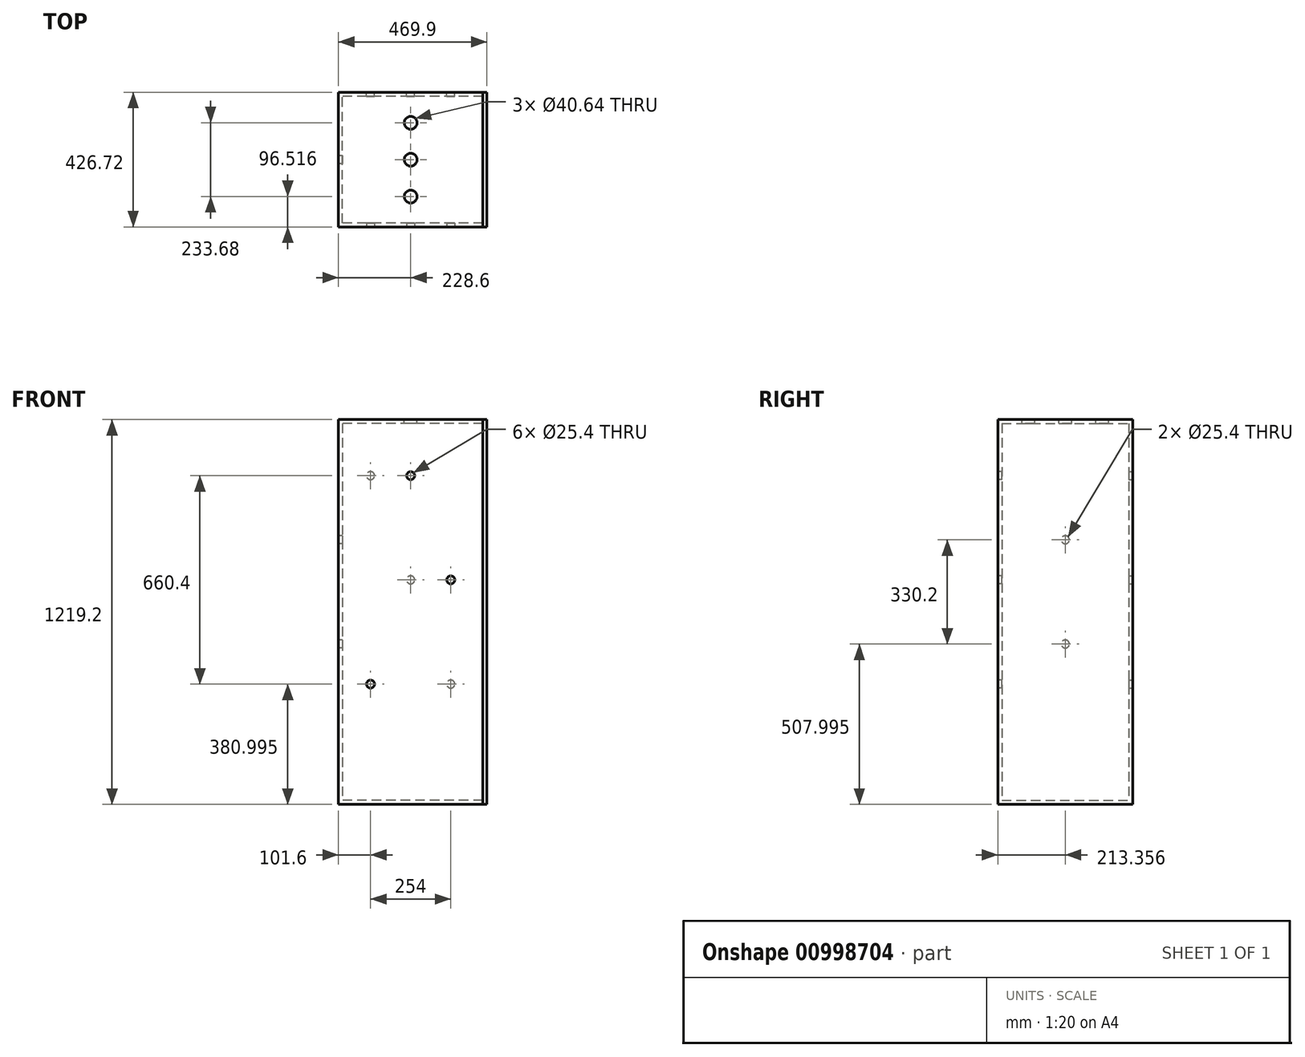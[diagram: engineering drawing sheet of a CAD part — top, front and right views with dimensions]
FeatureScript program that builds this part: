
annotation { "Feature Type Name" : "Feature", "Feature Type Description" : "" }
export const myFeature = defineFeature(function(context is Context, id is Id, definition is map)
    precondition{}
    {
        {
            var Q0;
            Q0=qCreatedBy(makeId("Right.planeOp"),FACE);
            var sketch = newSketch(context, id + "F0", { "sketchPlane" : qUnion([Q0])});
            skLineSegment(sketch, "E0.bottom", {"start": v(-375.54, 610.15) * mm, "end": v(51.18, 610.15) * mm});
            skLineSegment(sketch, "E0.top", {"start": v(-375.54, -609.05) * mm, "end": v(51.18, -609.05) * mm});
            skLineSegment(sketch, "E0.left", {"start": v(-375.54, 610.15) * mm, "end": v(-375.54, -609.05) * mm});
            skLineSegment(sketch, "E0.right", {"start": v(51.18, 610.15) * mm, "end": v(51.18, -609.05) * mm});
            skSolve(sketch);
        }
        {
            var Q0;
            Q0 = qSketchRegion(id + "F0", true);
            extrude(context, id + "F1", {"entities" : qUnion([Q0]), "depth" : 457.2 * mm, "offsetDistance" : 25.4 * mm});
        }
        {
            var Q0;
            Q0=makeQuery(id+"F1.opExtrude","CAP_FACE",FACE,{"disambiguationData":[OSD([sQuery(id+"F0.wireOp",EDGE,"E0.bottom"),sQuery(id+"F0.wireOp",EDGE,"E0.top"),sQuery(id+"F0.wireOp",EDGE,"E0.left"),sQuery(id+"F0.wireOp",EDGE,"E0.right")])],"isStart":false});
            shell(context, id + "F2", {"entities" : qUnion([Q0]), "thickness" : 12.7 * mm});
        }
        {
            var Q0;
            Q0=makeQuery(id+"F1.opExtrude","SWEPT_FACE",FACE,{"disambiguationData":[OSD([sQuery(id+"F0.wireOp",EDGE,"E0.bottom")])]});
            var sketch = newSketch(context, id + "F3", { "sketchPlane" : qUnion([Q0])});
            skLineSegment(sketch, "E1", {"start": v(228.6, 51.18) * mm, "end": v(228.6, -375.54) * mm, "construction": true});
            skLineSegment(sketch, "E2", {"start": v(228.6, -375.54) * mm, "end": v(228.6, -279.02) * mm, "construction": true});
            skCircle(sketch, "E3", {"center": v(228.6, -279.02) * mm, "radius": 20.32 * mm});
            skLineSegment(sketch, "E4", {"start": v(0, -162.18) * mm, "end": v(457.2, -162.18) * mm, "construction": true});
            skCircle(sketch, "E5.MirrorC", {"center": v(228.6, -45.34) * mm, "radius": 20.32 * mm});
            skCircle(sketch, "E6", {"center": v(228.6, -162.18) * mm, "radius": 20.32 * mm});
            skSolve(sketch);
        }
        {
            var Q0;
            Q0=sQuery(id+"F3.wireOp",VERTEX,"E6.center");
            var Q1;
            Q1=makeQuery(id+"F1.opExtrude","SWEPT_BODY",BODY,{"disambiguationData":[OSD([sQuery(id+"F0.wireOp",EDGE,"E0.bottom"),sQuery(id+"F0.wireOp",EDGE,"E0.top"),sQuery(id+"F0.wireOp",EDGE,"E0.left"),sQuery(id+"F0.wireOp",EDGE,"E0.right")])]});
            hole(context, id + "F4", {"style" : HoleStyle.SIMPLE, "endStyle" : HoleEndStyle.BLIND, "holeDiameter" : 40.64 * mm, "majorDiameter" : 6.35 * mm, "holeDepth" : 12.7 * mm, "isTappedThrough" : true, "tappedDepth" : 12.7 * mm, "tapClearance" : 3, "locations" : qUnion([Q0]), "scope" : qUnion([Q1])});
        }
        {
            var Q0;
            Q0=sQuery(id+"F3.wireOp",VERTEX,"E5.MirrorC.center");
            var Q1;
            Q1=makeQuery(id+"F1.opExtrude","SWEPT_BODY",BODY,{"disambiguationData":[OSD([sQuery(id+"F0.wireOp",EDGE,"E0.bottom"),sQuery(id+"F0.wireOp",EDGE,"E0.top"),sQuery(id+"F0.wireOp",EDGE,"E0.left"),sQuery(id+"F0.wireOp",EDGE,"E0.right")])]});
            hole(context, id + "F5", {"style" : HoleStyle.SIMPLE, "endStyle" : HoleEndStyle.BLIND, "holeDiameter" : 40.64 * mm, "majorDiameter" : 6.35 * mm, "holeDepth" : 12.7 * mm, "isTappedThrough" : true, "tappedDepth" : 12.7 * mm, "tapClearance" : 3, "locations" : qUnion([Q0]), "scope" : qUnion([Q1])});
        }
        {
            var Q0;
            Q0=sQuery(id+"F3.wireOp",VERTEX,"E2.end");
            var Q1;
            Q1=makeQuery(id+"F1.opExtrude","SWEPT_BODY",BODY,{"disambiguationData":[OSD([sQuery(id+"F0.wireOp",EDGE,"E0.bottom"),sQuery(id+"F0.wireOp",EDGE,"E0.top"),sQuery(id+"F0.wireOp",EDGE,"E0.left"),sQuery(id+"F0.wireOp",EDGE,"E0.right")])]});
            hole(context, id + "F6", {"style" : HoleStyle.SIMPLE, "endStyle" : HoleEndStyle.BLIND, "holeDiameter" : 40.64 * mm, "majorDiameter" : 6.35 * mm, "holeDepth" : 12.7 * mm, "isTappedThrough" : true, "tappedDepth" : 12.7 * mm, "tapClearance" : 3, "locations" : qUnion([Q0]), "scope" : qUnion([Q1])});
        }
        {
            var Q0;
            Q0=makeQuery(id+"F1.opExtrude","CAP_FACE",FACE,{"disambiguationData":[OSD([sQuery(id+"F0.wireOp",EDGE,"E0.bottom"),sQuery(id+"F0.wireOp",EDGE,"E0.top"),sQuery(id+"F0.wireOp",EDGE,"E0.left"),sQuery(id+"F0.wireOp",EDGE,"E0.right")])],"isStart":false});
            var sketch = newSketch(context, id + "F7", { "sketchPlane" : qUnion([Q0])});
            skLineSegment(sketch, "E7.bottom", {"start": v(-375.54, 610.15) * mm, "end": v(51.18, 610.15) * mm});
            skLineSegment(sketch, "E7.top", {"start": v(-375.54, -609.05) * mm, "end": v(51.18, -609.05) * mm});
            skLineSegment(sketch, "E7.left", {"start": v(-375.54, 610.15) * mm, "end": v(-375.54, -609.05) * mm});
            skLineSegment(sketch, "E7.right", {"start": v(51.18, 610.15) * mm, "end": v(51.18, -609.05) * mm});
            skSolve(sketch);
        }
        {
            var Q0;
            Q0 = qSketchRegion(id + "F7", true);
            extrude(context, id + "F8", {"entities" : qUnion([Q0]), "depth" : 12.7 * mm, "offsetDistance" : 25.4 * mm});
        }
        {
            var Q0;
            Q0=makeQuery(id+"F1.opExtrude","SWEPT_FACE",FACE,{"disambiguationData":[OSD([sQuery(id+"F0.wireOp",EDGE,"E0.left")])]});
            var sketch = newSketch(context, id + "F9", { "sketchPlane" : qUnion([Q0])});
            skLineSegment(sketch, "E8", {"start": v(0, 610.15) * mm, "end": v(101.6, 610.15) * mm, "construction": true});
            skLineSegment(sketch, "E9", {"start": v(101.6, 610.15) * mm, "end": v(355.6, 610.15) * mm, "construction": true});
            skLineSegment(sketch, "E10", {"start": v(355.6, 610.15) * mm, "end": v(457.2, 610.15) * mm, "construction": true});
            skLineSegment(sketch, "E11", {"start": v(228.6, 610.15) * mm, "end": v(228.6, -609.05) * mm, "construction": true});
            skLineSegment(sketch, "E12", {"start": v(101.6, 610.15) * mm, "end": v(101.6, -609.05) * mm, "construction": true});
            skLineSegment(sketch, "E13", {"start": v(355.6, 610.15) * mm, "end": v(355.6, -609.05) * mm, "construction": true});
            skLineSegment(sketch, "E14", {"start": v(101.6, -609.05) * mm, "end": v(101.6, -228.05) * mm, "construction": true});
            skLineSegment(sketch, "E15", {"start": v(355.6, 610.15) * mm, "end": v(355.6, 102.15) * mm, "construction": true});
            skLineSegment(sketch, "E16", {"start": v(228.6, 610.15) * mm, "end": v(228.6, 432.35) * mm, "construction": true});
            skCircle(sketch, "E17", {"center": v(101.6, -228.05) * mm, "radius": 13.97 * mm});
            skCircle(sketch, "E18", {"center": v(228.6, 432.35) * mm, "radius": 13.97 * mm});
            skCircle(sketch, "E19", {"center": v(355.6, 102.15) * mm, "radius": 13.97 * mm});
            skSolve(sketch);
        }
        {
            var Q0;
            Q0=sQuery(id+"F9.wireOp",VERTEX,"E14.end");
            var Q1;
            Q1=makeQuery(id+"F1.opExtrude","SWEPT_BODY",BODY,{"disambiguationData":[OSD([sQuery(id+"F0.wireOp",EDGE,"E0.bottom"),sQuery(id+"F0.wireOp",EDGE,"E0.top"),sQuery(id+"F0.wireOp",EDGE,"E0.left"),sQuery(id+"F0.wireOp",EDGE,"E0.right")])]});
            hole(context, id + "F10", {"style" : HoleStyle.SIMPLE, "endStyle" : HoleEndStyle.BLIND, "holeDiameter" : 25.4 * mm, "majorDiameter" : 6.35 * mm, "holeDepth" : 12.7 * mm, "isTappedThrough" : true, "tappedDepth" : 12.7 * mm, "tapClearance" : 3, "locations" : qUnion([Q0]), "scope" : qUnion([Q1])});
        }
        {
            var Q0;
            Q0=sQuery(id+"F9.wireOp",VERTEX,"E16.end");
            var Q1;
            Q1=sQuery(id+"F9.wireOp",VERTEX,"E15.end");
            var Q2;
            Q2=makeQuery(id+"F1.opExtrude","SWEPT_BODY",BODY,{"disambiguationData":[OSD([sQuery(id+"F0.wireOp",EDGE,"E0.bottom"),sQuery(id+"F0.wireOp",EDGE,"E0.top"),sQuery(id+"F0.wireOp",EDGE,"E0.left"),sQuery(id+"F0.wireOp",EDGE,"E0.right")])]});
            hole(context, id + "F11", {"style" : HoleStyle.SIMPLE, "endStyle" : HoleEndStyle.BLIND, "holeDiameter" : 25.4 * mm, "majorDiameter" : 6.35 * mm, "holeDepth" : 12.7 * mm, "isTappedThrough" : true, "tappedDepth" : 12.7 * mm, "tapClearance" : 3, "locations" : qUnion([Q0, Q1]), "scope" : qUnion([Q2])});
        }
        {
            var Q0;
            Q0=makeQuery(id+"F1.opExtrude","CAP_FACE",FACE,{"disambiguationData":[OSD([sQuery(id+"F0.wireOp",EDGE,"E0.bottom"),sQuery(id+"F0.wireOp",EDGE,"E0.top"),sQuery(id+"F0.wireOp",EDGE,"E0.left"),sQuery(id+"F0.wireOp",EDGE,"E0.right")])],"isStart":true});
            var sketch = newSketch(context, id + "F12", { "sketchPlane" : qUnion([Q0])});
            skLineSegment(sketch, "E20", {"start": v(162.18, 610.15) * mm, "end": v(162.18, -609.05) * mm, "construction": true});
            skLineSegment(sketch, "E21", {"start": v(162.18, -609.05) * mm, "end": v(162.18, 229.15) * mm, "construction": true});
            skLineSegment(sketch, "E22", {"start": v(162.18, -609.05) * mm, "end": v(162.18, -101.05) * mm, "construction": true});
            skSolve(sketch);
        }
        {
            var Q0;
            Q0=sQuery(id+"F12.wireOp",VERTEX,"E21.end");
            var Q1;
            Q1=sQuery(id+"F12.wireOp",VERTEX,"E22.end");
            var Q2;
            Q2=makeQuery(id+"F1.opExtrude","SWEPT_BODY",BODY,{"disambiguationData":[OSD([sQuery(id+"F0.wireOp",EDGE,"E0.bottom"),sQuery(id+"F0.wireOp",EDGE,"E0.top"),sQuery(id+"F0.wireOp",EDGE,"E0.left"),sQuery(id+"F0.wireOp",EDGE,"E0.right")])]});
            hole(context, id + "F13", {"style" : HoleStyle.SIMPLE, "endStyle" : HoleEndStyle.BLIND, "holeDiameter" : 25.4 * mm, "majorDiameter" : 6.35 * mm, "holeDepth" : 12.7 * mm, "isTappedThrough" : true, "tappedDepth" : 12.7 * mm, "tapClearance" : 3, "locations" : qUnion([Q0, Q1]), "scope" : qUnion([Q2])});
        }
        {
            var Q0;
            Q0=makeQuery(id+"F1.opExtrude","SWEPT_FACE",FACE,{"disambiguationData":[OSD([sQuery(id+"F0.wireOp",EDGE,"E0.right")])]});
            var sketch = newSketch(context, id + "F14", { "sketchPlane" : qUnion([Q0])});
            skLineSegment(sketch, "E23", {"start": v(-457.2, 610.15) * mm, "end": v(-355.6, 610.15) * mm, "construction": true});
            skLineSegment(sketch, "E24", {"start": v(0, 610.15) * mm, "end": v(-101.6, 610.15) * mm, "construction": true});
            skLineSegment(sketch, "E25", {"start": v(-355.6, 610.15) * mm, "end": v(-355.6, -609.05) * mm, "construction": true});
            skLineSegment(sketch, "E26", {"start": v(-228.6, 610.15) * mm, "end": v(-228.6, -609.05) * mm, "construction": true});
            skLineSegment(sketch, "E27", {"start": v(-101.6, 610.15) * mm, "end": v(-101.6, -609.05) * mm, "construction": true});
            skLineSegment(sketch, "E28", {"start": v(-355.6, 610.15) * mm, "end": v(-355.6, -228.05) * mm, "construction": true});
            skLineSegment(sketch, "E29", {"start": v(-228.6, 610.15) * mm, "end": v(-228.6, 102.15) * mm, "construction": true});
            skLineSegment(sketch, "E30", {"start": v(-101.6, 610.15) * mm, "end": v(-101.6, 432.35) * mm, "construction": true});
            skSolve(sketch);
        }
        {
            var Q0;
            Q0=sQuery(id+"F14.wireOp",VERTEX,"E30.end");
            var Q1;
            Q1=sQuery(id+"F14.wireOp",VERTEX,"E29.end");
            var Q2;
            Q2=sQuery(id+"F14.wireOp",VERTEX,"E28.end");
            var Q3;
            Q3=makeQuery(id+"F1.opExtrude","SWEPT_BODY",BODY,{"disambiguationData":[OSD([sQuery(id+"F0.wireOp",EDGE,"E0.bottom"),sQuery(id+"F0.wireOp",EDGE,"E0.top"),sQuery(id+"F0.wireOp",EDGE,"E0.left"),sQuery(id+"F0.wireOp",EDGE,"E0.right")])]});
            hole(context, id + "F15", {"style" : HoleStyle.SIMPLE, "endStyle" : HoleEndStyle.BLIND, "holeDiameter" : 25.4 * mm, "majorDiameter" : 6.35 * mm, "holeDepth" : 12.7 * mm, "isTappedThrough" : true, "tappedDepth" : 12.7 * mm, "tapClearance" : 3, "locations" : qUnion([Q0, Q1, Q2]), "scope" : qUnion([Q3])});
        }
    });
